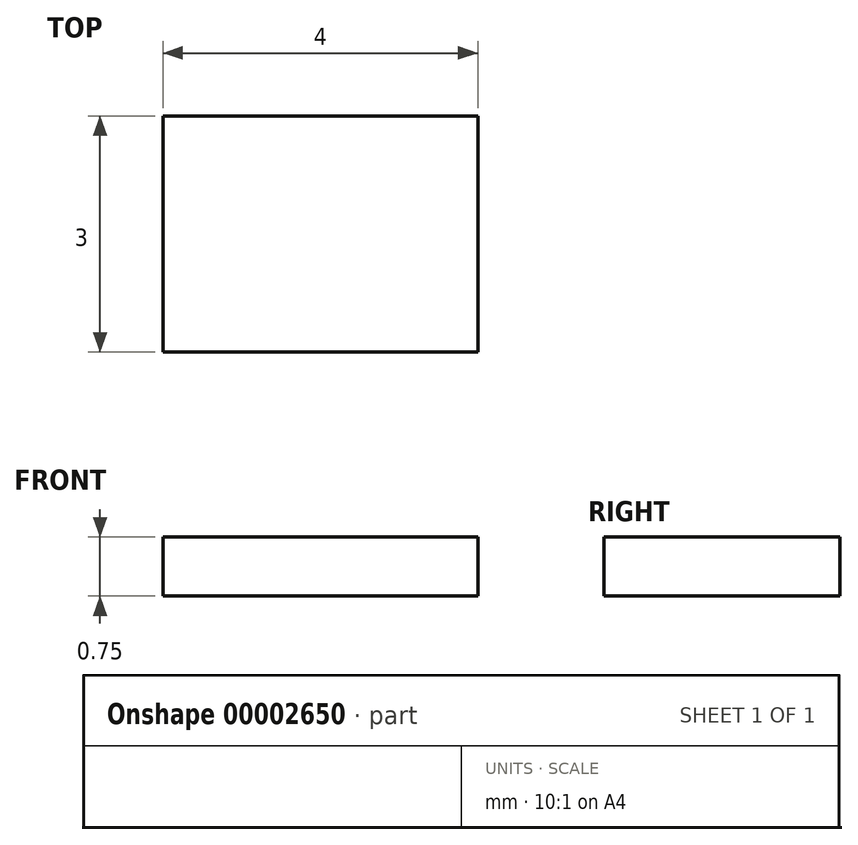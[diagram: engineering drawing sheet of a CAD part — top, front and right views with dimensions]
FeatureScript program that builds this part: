
annotation { "Feature Type Name" : "Feature", "Feature Type Description" : "" }
export const myFeature = defineFeature(function(context is Context, id is Id, definition is map)
    precondition{}
    {
        {
            var Q0;
            Q0=qCreatedBy(makeId("Top.planeOp"),FACE);
            var sketch = newSketch(context, id + "F0", { "sketchPlane" : qUnion([Q0])});
            skLineSegment(sketch, "E0.bottom", {"start": v(-1.03, 5.39) * mm, "end": v(2.97, 5.39) * mm});
            skLineSegment(sketch, "E0.top", {"start": v(-1.03, 2.39) * mm, "end": v(2.97, 2.39) * mm});
            skLineSegment(sketch, "E0.left", {"start": v(-1.03, 5.39) * mm, "end": v(-1.03, 2.39) * mm});
            skLineSegment(sketch, "E0.right", {"start": v(2.97, 5.39) * mm, "end": v(2.97, 2.39) * mm});
            skSolve(sketch);
        }
        {
            var Q0;
            Q0=makeQuery(id+"F0.imprint","IMPRINT",FACE,{"disambiguationData":[TD([[makeQuery(id+"F0.imprint","IMPRINT",EDGE,{"derivedFrom":sQuery(id+"F0.wireOp",EDGE,"E0.bottom")}),-1.0]])]});
            extrude(context, id + "F1", {"entities" : qUnion([Q0]), "depth" : .75 * mm});
        }
    });
